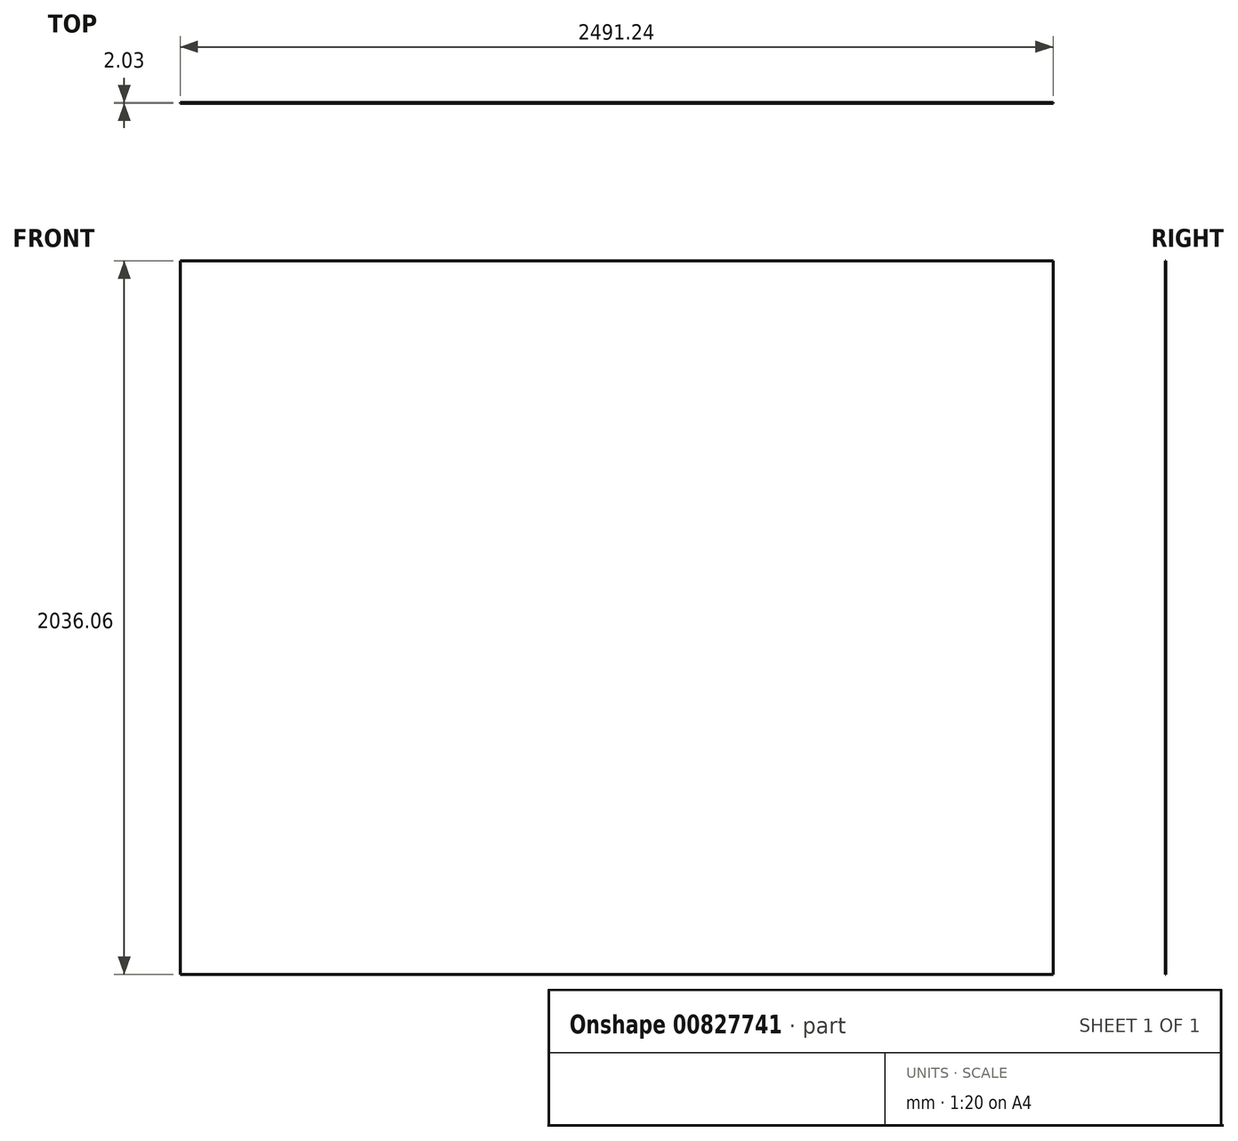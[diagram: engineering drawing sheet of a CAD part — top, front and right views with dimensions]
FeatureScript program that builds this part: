
annotation { "Feature Type Name" : "Feature", "Feature Type Description" : "" }
export const myFeature = defineFeature(function(context is Context, id is Id, definition is map)
    precondition{}
    {
        {
            var Q0;
            Q0=qCreatedBy(makeId("Front.planeOp"),FACE);
            var sketch = newSketch(context, id + "F0", { "sketchPlane" : qUnion([Q0])});
            skLineSegment(sketch, "E0.bottom", {"start": v(-2409.49, 217.26) * mm, "end": v(81.75, 217.26) * mm});
            skLineSegment(sketch, "E0.top", {"start": v(-2409.49, -1818.8) * mm, "end": v(81.75, -1818.8) * mm});
            skLineSegment(sketch, "E0.left", {"start": v(-2409.49, 217.26) * mm, "end": v(-2409.49, -1818.8) * mm});
            skLineSegment(sketch, "E0.right", {"start": v(81.75, 217.26) * mm, "end": v(81.75, -1818.8) * mm});
            skSolve(sketch);
        }
        {
            var Q0;
            Q0=qSketchRegion(id+"F0",true);
            extrude(context, id + "F1", {"entities" : qUnion([Q0]), "depth" : 2.03 * mm, "offsetDistance" : 25.4 * mm});
        }
    });
